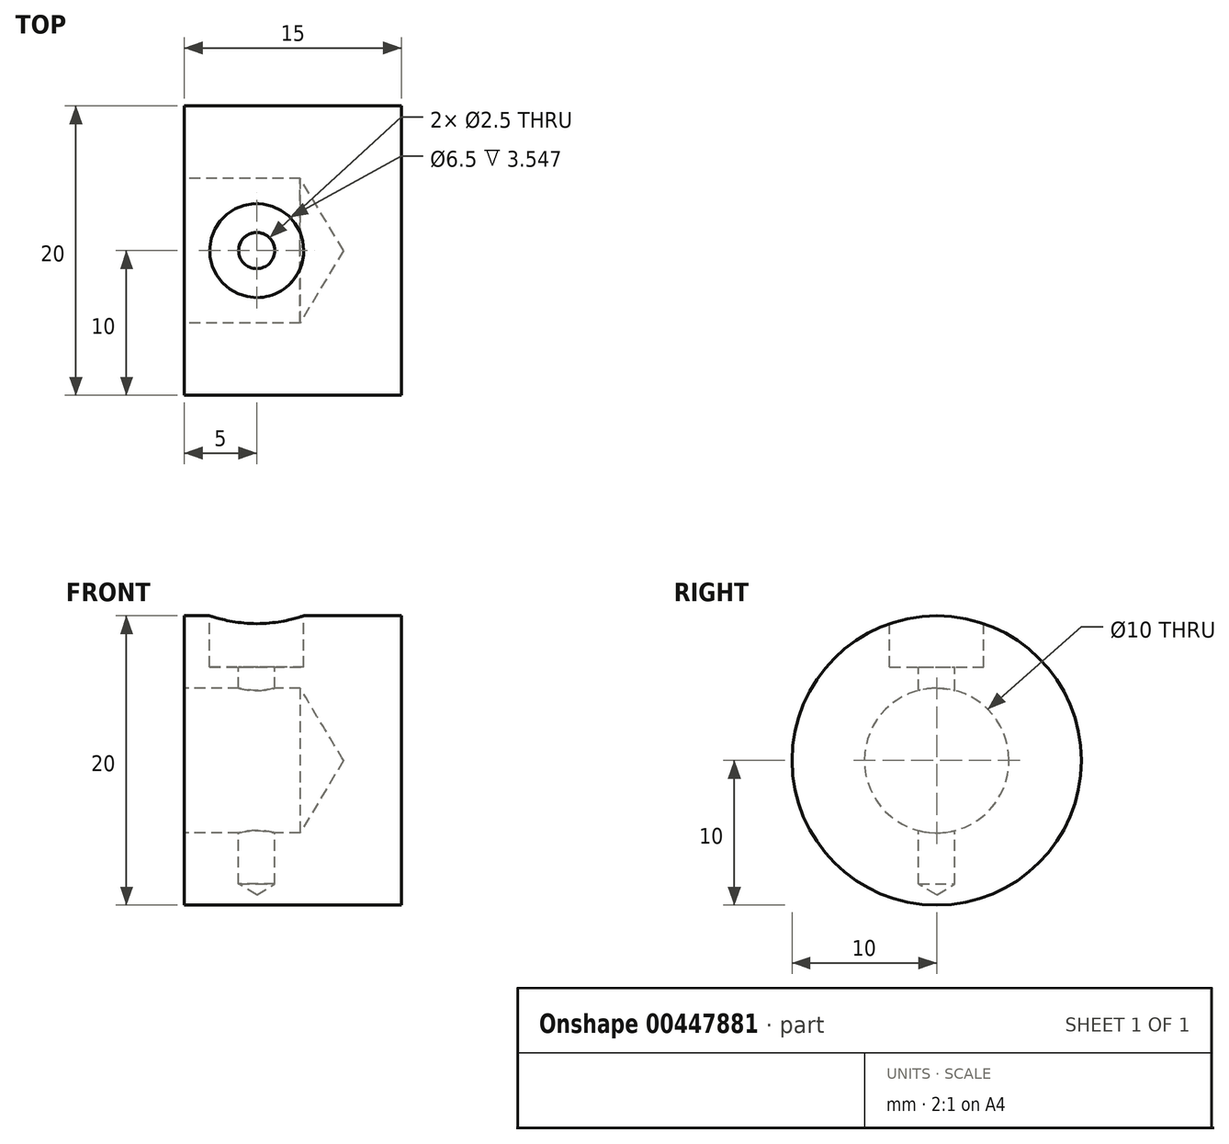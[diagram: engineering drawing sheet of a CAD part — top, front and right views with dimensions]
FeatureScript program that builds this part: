
annotation { "Feature Type Name" : "Feature", "Feature Type Description" : "" }
export const myFeature = defineFeature(function(context is Context, id is Id, definition is map)
    precondition{}
    {
        {
            var Q0;
            Q0=qCreatedBy(makeId("Right.planeOp"),FACE);
            var sketch = newSketch(context, id + "F0", { "sketchPlane" : qUnion([Q0])});
            skCircle(sketch, "E0", {"center": v(0, 0) * mm, "radius": 10 * mm});
            skPoint(sketch, "E1", {"position": v(0, -10) * mm});
            skPoint(sketch, "E2", {"position": v(0, 10) * mm});
            skSolve(sketch);
        }
        {
            var Q0;
            Q0=makeQuery(id+"F0.imprint","IMPRINT",FACE,{"disambiguationData":[TD([[makeQuery(id+"F0.imprint","IMPRINT",EDGE,{"derivedFrom":sQuery(id+"F0.wireOp",EDGE,"E0")}),1.0]])]});
            extrude(context, id + "F1", {"entities" : qUnion([Q0]), "depth" : 15 * mm});
        }
        {
            var Q0;
            Q0=sQuery(id+"F0.wireOp",VERTEX,"E0.center");
            var Q1;
            Q1=makeQuery(id+"F1.opExtrude","SWEPT_BODY",BODY,{"disambiguationData":[OSD([sQuery(id+"F0.wireOp",EDGE,"E0")])]});
            hole(context, id + "F2", {"style" : HoleStyle.SIMPLE, "endStyle" : HoleEndStyle.BLIND, "oppositeDirection" : true, "standardTappedOrClearance" : lookupTablePath({ "standard" : "ISO", "size" : "10", "type" : "Drilled" }), "standardBlindInLast" : lookupTablePath({ "standard" : "ISO", "size" : "10", "type" : "Drilled" }), "holeDiameter" : 10 * mm, "holeDepth" : 8 * mm, "isTappedThrough" : true, "tappedDepth" : 12 * mm, "tapClearance" : 3, "locations" : qUnion([Q0]), "scope" : qUnion([Q1])});
        }
        {
            var Q0;
            Q0=qCreatedBy(makeId("Front.planeOp"),FACE);
            var sketch = newSketch(context, id + "F3", { "sketchPlane" : qUnion([Q0])});
            skLineSegment(sketch, "E3", {"start": v(0, 10) * mm, "end": v(15, 10) * mm, "construction": true});
            skLineSegment(sketch, "E4", {"start": v(15, -10) * mm, "end": v(0, -10) * mm, "construction": true});
            skLineSegment(sketch, "E5.0", {"start": v(0, 10) * mm, "end": v(0, -10) * mm, "construction": true});
            skLineSegment(sketch, "E6.0", {"start": v(15, 10) * mm, "end": v(15, -10) * mm, "construction": true});
            skPoint(sketch, "E7", {"position": v(5, 10) * mm});
            skPoint(sketch, "E8", {"position": v(5, -10) * mm});
            skLineSegment(sketch, "E9", {"start": v(5, 10) * mm, "end": v(5, -10) * mm, "construction": true});
            skSolve(sketch);
        }
        {
            var Q0;
            Q0=sQuery(id+"F3.wireOp",EDGE,"E3");
            cPlane(context, id + "F4", {"entities" : qUnion([Q0]), "cplaneType" : CPlaneType.LINE_ANGLE, "offset" : 0 * mm, "angle" : 90 * degree, "width" : 150 * mm, "height" : 150 * mm});
        }
        {
            var Q0;
            Q0=qCreatedBy(id+"F4.planeOp",FACE);
            var sketch = newSketch(context, id + "F5", { "sketchPlane" : qUnion([Q0])});
            skPoint(sketch, "E10", {"position": v(5, 0) * mm});
            skSolve(sketch);
        }
        {
            var Q0;
            Q0=sQuery(id+"F5.wireOp",VERTEX,"E10");
            var Q1;
            Q1=makeQuery(id+"F1.opExtrude","SWEPT_BODY",BODY,{"disambiguationData":[OSD([sQuery(id+"F0.wireOp",EDGE,"E0")])]});
            hole(context, id + "F6", {"style" : HoleStyle.C_BORE, "endStyle" : HoleEndStyle.BLIND, "standardTappedOrClearance" : lookupTablePath({ "standard" : "ISO", "engagement" : "75%", "pitch" : "0.5 mm", "size" : "M3", "type" : "Tapped" }), "standardBlindInLast" : lookupTablePath({ "standard" : "ISO", "engagement" : "75%", "pitch" : "0.5 mm", "size" : "M3", "type" : "Tapped" }), "holeDiameter" : 2.5 * mm, "cBoreDiameter" : 6.5 * mm, "cBoreDepth" : 3 * mm, "showTappedDepth" : true, "holeDepth" : 18 * mm, "isTappedThrough" : true, "tappedDepth" : 12 * mm, "tapClearance" : 12, "locations" : qUnion([Q0]), "scope" : qUnion([Q1]), "majorDiameter" : 3 * mm});
        }
    });
